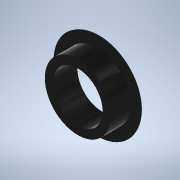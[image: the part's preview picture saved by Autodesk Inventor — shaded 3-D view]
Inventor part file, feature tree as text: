
AUTODESK INVENTOR PART (.ipt)
format: ipt  version: 2020 (Build 240168000, 168)  size: 134,656 bytes
history: native  units: mm
features: revolve x1, sketch x1
ambient origin geometry x8: Origin, YZ Plane, XZ Plane, XY Plane, X Axis, Y Axis, Z Axis, Center Point
bodies: Volumenkörper1 (feature_tree)
feature tree (2):
  revolve  "Umdrehung1"
  sketch  "Skizze1"  dims[d0=6.8mm d1=5.1mm d2=1.0mm d3=9.0mm d4=1.0mm d6=4.0mm d7=90.0deg d8=0.5mm]
